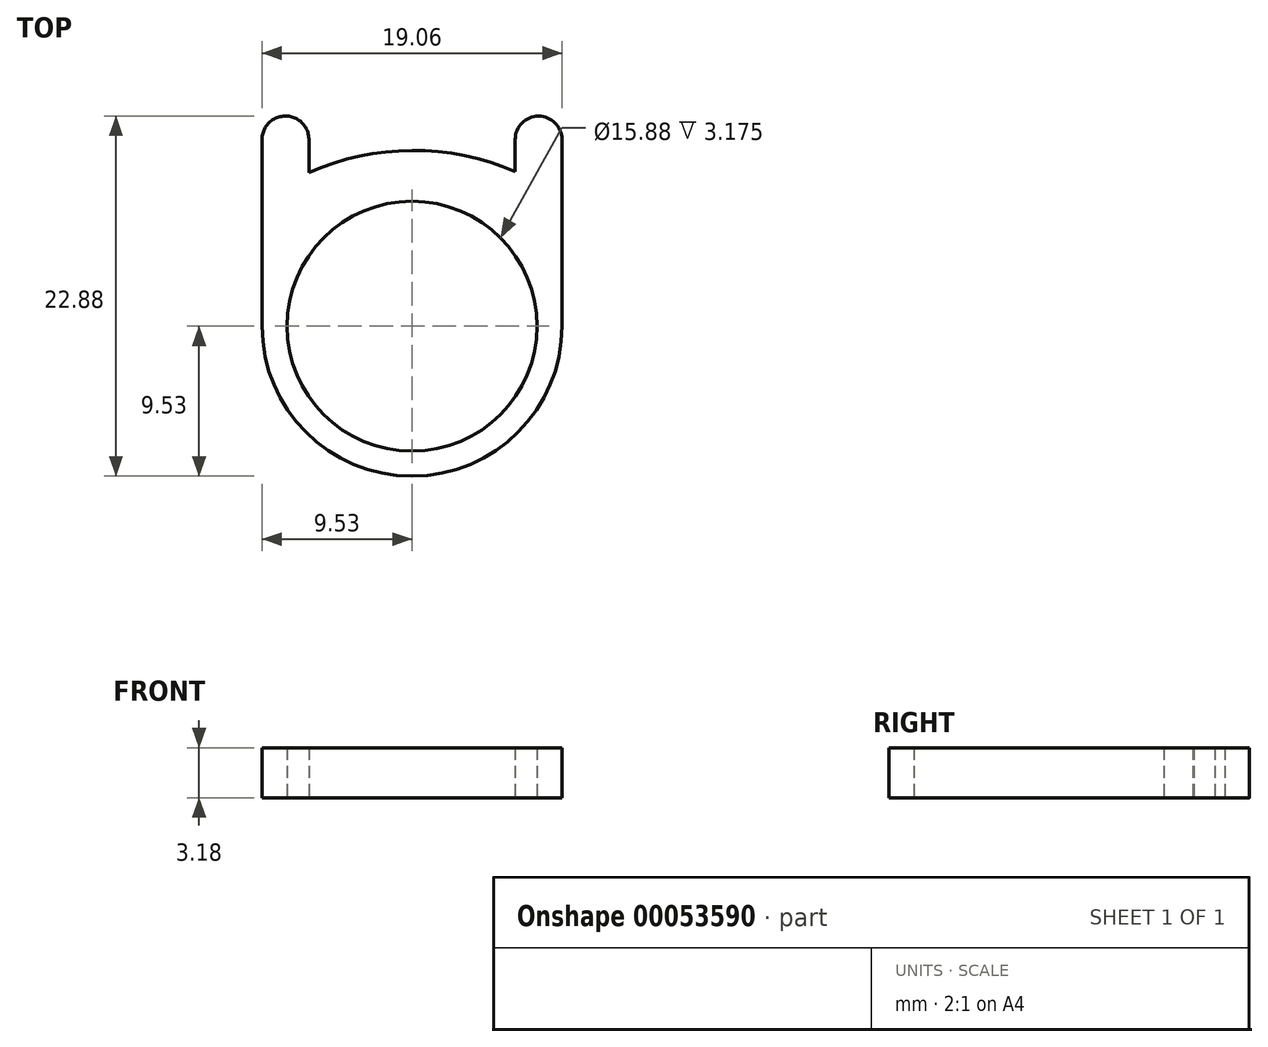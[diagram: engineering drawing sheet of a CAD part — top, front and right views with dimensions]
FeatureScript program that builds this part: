
annotation { "Feature Type Name" : "Feature", "Feature Type Description" : "" }
export const myFeature = defineFeature(function(context is Context, id is Id, definition is map)
    precondition{}
    {
        {
            var Q0;
            Q0=qCreatedBy(makeId("Top.planeOp"),FACE);
            var sketch = newSketch(context, id + "F0", { "sketchPlane" : qUnion([Q0])});
            skCircle(sketch, "E0", {"center": v(0, 0) * mm, "radius": 7.94 * mm});
            skCircle(sketch, "E1", {"center": v(0, 0) * mm, "radius": 9.53 * mm});
            skLineSegment(sketch, "E2", {"start": v(9.53, 0) * mm, "end": v(9.53, 11.86) * mm});
            skLineSegment(sketch, "E3", {"start": v(9.52, 11.86) * mm, "end": v(6.55, 11.86) * mm});
            skLineSegment(sketch, "E4", {"start": v(6.55, 11.86) * mm, "end": v(6.55, 9.83) * mm});
            skLineSegment(sketch, "E5", {"start": v(-6.55, 9.77) * mm, "end": v(-6.55, 11.8) * mm});
            skLineSegment(sketch, "E6", {"start": v(-9.53, 0) * mm, "end": v(-9.53, 11.87) * mm});
            skLineSegment(sketch, "E7", {"start": v(-9.53, 11.87) * mm, "end": v(-6.55, 11.8) * mm});
            skArc(sketch, "E8", {"start": v(6.55, 9.83) * mm, "mid": v(0, 11.16) * mm, "end": v(-6.55, 9.77) * mm});
            skLineSegment(sketch, "E9", {"start": v(-9.53, 0) * mm, "end": v(-7.94, 0) * mm});
            skArc(sketch, "E10", {"start": v(-6.55, 11.8) * mm, "mid": v(-8, 13.35) * mm, "end": v(-9.53, 11.87) * mm});
            skArc(sketch, "E11", {"start": v(9.52, 11.86) * mm, "mid": v(8.04, 13.35) * mm, "end": v(6.55, 11.86) * mm});
            skSolve(sketch);
        }
        {
            var Q0;
            Q0 = qSketchRegion(id + "F0", true);
            extrude(context, id + "F1", {"entities" : qUnion([Q0]), "depth" : 3.17 * mm});
        }
    });
